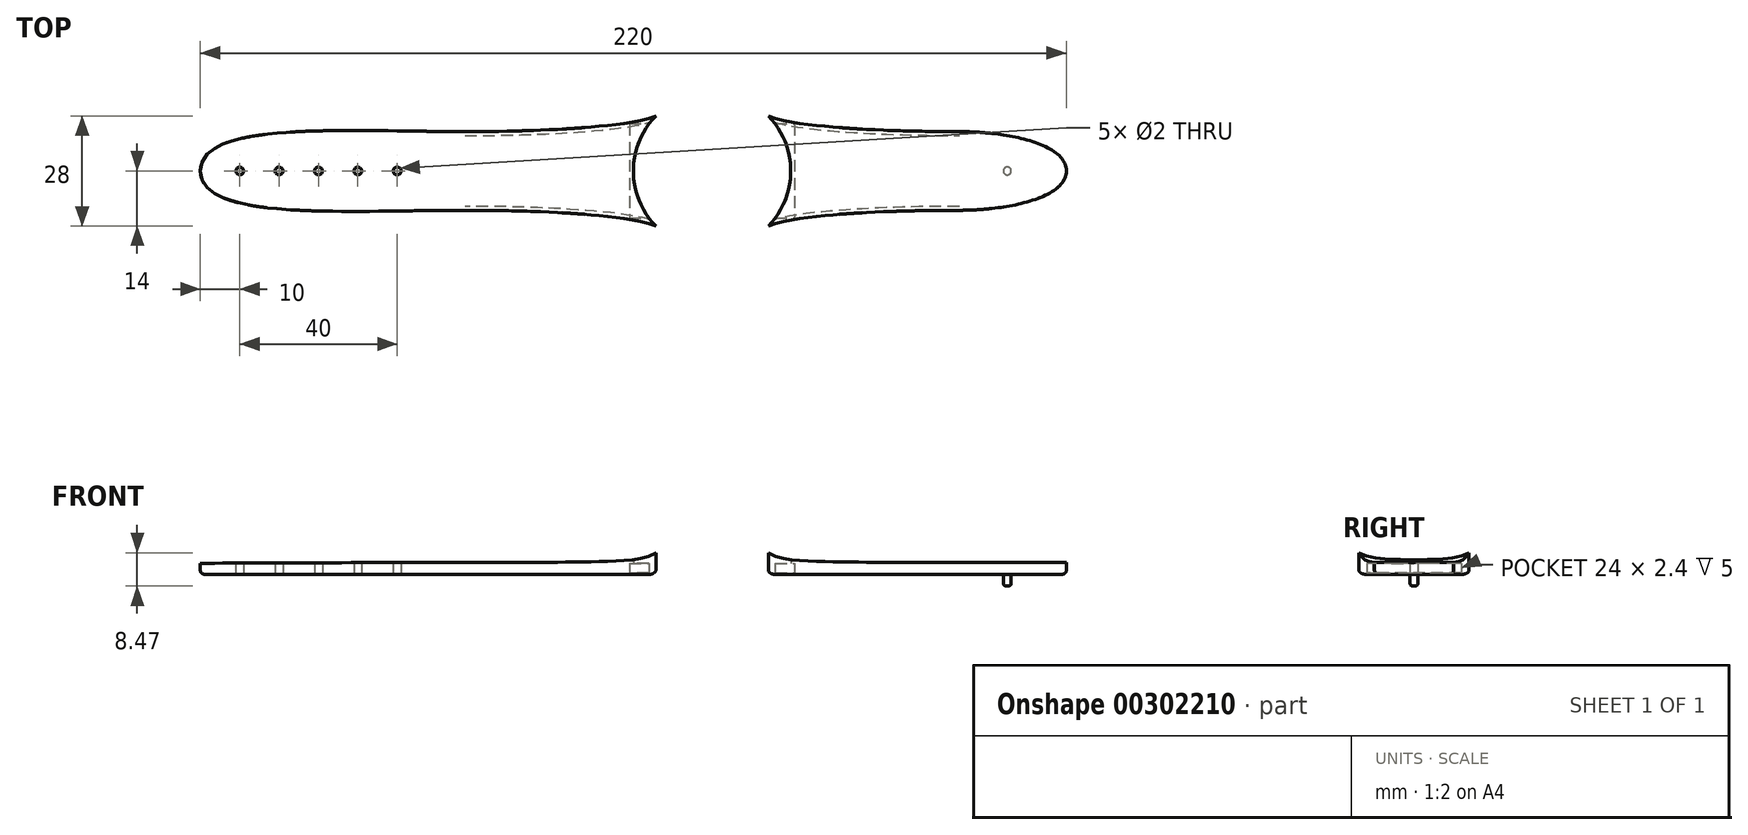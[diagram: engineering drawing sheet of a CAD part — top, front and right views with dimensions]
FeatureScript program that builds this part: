
annotation { "Feature Type Name" : "Feature", "Feature Type Description" : "" }
export const myFeature = defineFeature(function(context is Context, id is Id, definition is map)
    precondition{}
    {
        {
            var Q0;
            Q0=qCreatedBy(makeId("Top.planeOp"),FACE);
            var sketch = newSketch(context, id + "F0", { "sketchPlane" : qUnion([Q0])});
            skArc(sketch, "E0", {"start": v(-14.28, 14) * mm, "mid": v(-20, 0) * mm, "end": v(-14.28, -14) * mm});
            skFitSpline(sketch, "E1", {"points": [v(-14.28, 14) * mm, v(-62.8, 10) * mm], "startDerivative": vector(-9.22, -5.33) * mm, "endDerivative": vector(-87.74, 0) * mm});
            skLineSegment(sketch, "E2", {"start": v(-62.8, 10) * mm, "end": v(-62.8, 10) * mm});
            skFitSpline(sketch, "E3", {"points": [v(-62.8, 10) * mm, v(-130, 0) * mm], "startDerivative": vector(-91.88, 0) * mm, "endDerivative": vector(0, -38.55) * mm});
            skFitSpline(sketch, "E4.MirrorCS", {"points": [v(-14.28, -14) * mm, v(-62.8, -10) * mm], "startDerivative": vector(-9.22, 5.33) * mm, "endDerivative": vector(-87.74, 0) * mm});
            skLineSegment(sketch, "E5.MirrorCS", {"start": v(-62.8, -10) * mm, "end": v(-62.8, -10) * mm});
            skFitSpline(sketch, "E6.MirrorCS", {"points": [v(-62.8, -10) * mm, v(-130, 0) * mm], "startDerivative": vector(-91.88, 0) * mm, "endDerivative": vector(0, 38.55) * mm});
            skArc(sketch, "E7.MirrorCS", {"start": v(14.28, 14) * mm, "mid": v(20, 0) * mm, "end": v(14.28, -14) * mm});
            skFitSpline(sketch, "E8.MirrorCS", {"points": [v(14.28, 14) * mm, v(62.8, 10) * mm], "startDerivative": vector(9.22, -5.33) * mm, "endDerivative": vector(87.74, 0) * mm});
            skFitSpline(sketch, "E9.MirrorCS", {"points": [v(14.28, -14) * mm, v(62.8, -10) * mm], "startDerivative": vector(9.22, 5.33) * mm, "endDerivative": vector(87.74, 0) * mm});
            skLineSegment(sketch, "E10", {"start": v(62.8, 10) * mm, "end": v(62.8, 10) * mm});
            skLineSegment(sketch, "E11.MirrorCS", {"start": v(62.8, -10) * mm, "end": v(62.8, -10) * mm});
            skFitSpline(sketch, "E12.MirrorCS", {"points": [v(62.8, -10) * mm, v(90, 0) * mm], "startDerivative": vector(33.22, 0) * mm, "endDerivative": vector(0, 21.8) * mm});
            skFitSpline(sketch, "E13.MirrorCS", {"points": [v(62.8, 10) * mm, v(90, 0) * mm], "startDerivative": vector(33.22, 0) * mm, "endDerivative": vector(0, -21.8) * mm});
            skSolve(sketch);
        }
        {
            var Q0;
            Q0 = qSketchRegion(id + "F0", true);
            extrude(context, id + "F1", {"entities" : qUnion([Q0]), "depth" : (5.5) * mm});
        }
        {
            var Q0;
            Q0=qCreatedBy(makeId("Front.planeOp"),FACE);
            var sketch = newSketch(context, id + "F2", { "sketchPlane" : qUnion([Q0])});
            skLineSegment(sketch, "E14", {"start": v(-133.54, 2.78) * mm, "end": v(-133.54, 10.44) * mm});
            skLineSegment(sketch, "E15", {"start": v(-14.23, 5.5) * mm, "end": v(-25.17, 14.96) * mm});
            skLineSegment(sketch, "E16", {"start": v(-25.17, 14.96) * mm, "end": v(-133.54, 10.44) * mm});
            skLineSegment(sketch, "E17", {"start": v(14.23, 5.5) * mm, "end": v(22.62, 12.49) * mm});
            skLineSegment(sketch, "E18", {"start": v(22.62, 12.49) * mm, "end": v(93.9, 5.99) * mm});
            skPoint(sketch, "E19", {"position": v(-133.54, 2.78) * mm});
            skFitSpline(sketch, "E20.MirrorCS", {"points": [v(14.23, 5.5) * mm, v(80, 3) * mm], "startDerivative": vector(15.03, -7.53) * mm, "endDerivative": vector(188.68, 0) * mm});
            skFitSpline(sketch, "E21.MirrorCS", {"points": [v(-14.23, 5.5) * mm, v(-80, 3) * mm], "startDerivative": vector(-15.03, -7.53) * mm, "endDerivative": vector(-188.68, 0) * mm});
            skLineSegment(sketch, "E22.MirrorCS", {"start": v(-80, 3) * mm, "end": v(-133.54, 2.78) * mm});
            skLineSegment(sketch, "E23", {"start": v(80, 3) * mm, "end": v(80, 3) * mm});
            skLineSegment(sketch, "E24", {"start": v(80, 3) * mm, "end": v(92.32, 3) * mm});
            skLineSegment(sketch, "E25", {"start": v(92.32, 3) * mm, "end": v(93.9, 5.99) * mm});
            skSolve(sketch);
        }
        {
            var Q0;
            Q0 = qSketchRegion(id + "F2", true);
            extrude(context, id + "F3", {"entities" : qUnion([Q0]), "operationType" : NewBodyOperationType.REMOVE, "endBound" : BoundingType.SYMMETRIC, "oppositeDirection" : true, "depth" : 40 * mm});
        }
        {
            var Q0;
            Q0=makeQuery(id+"F3.boolean.opBoolean","INTERSECT",EDGE,{"derivedFrom":[makeQuery(id+"F1.opExtrude","SWEPT_FACE",FACE,{"disambiguationData":[OSD([sQuery(id+"F0.wireOp",EDGE,"E1")])]}),makeQuery(id+"F3.opExtrude","SWEPT_FACE",FACE,{"disambiguationData":[OSD([sQuery(id+"F2.wireOp",EDGE,"ddad4ba2-1875-45fb-a996-aad7ab552623")])]})]});
            var Q1;
            Q1=makeQuery(id+"F3.boolean.opBoolean","INTERSECT",EDGE,{"derivedFrom":[makeQuery(id+"F1.opExtrude","SWEPT_FACE",FACE,{"disambiguationData":[OSD([sQuery(id+"F0.wireOp",EDGE,"E3")])]}),makeQuery(id+"F3.opExtrude","SWEPT_FACE",FACE,{"disambiguationData":[OSD([sQuery(id+"F2.wireOp",EDGE,"ddad4ba2-1875-45fb-a996-aad7ab552623")])]})]});
            var Q2;
            Q2=makeQuery(id+"F1.opExtrude","CAP_EDGE",EDGE,{"disambiguationData":[OSD([sQuery(id+"F0.wireOp",EDGE,"E1")])],"isStart":true});
            var Q3;
            Q3=makeQuery(id+"F1.opExtrude","CAP_EDGE",EDGE,{"disambiguationData":[OSD([sQuery(id+"F0.wireOp",EDGE,"E8.MirrorCS")])],"isStart":true});
            var Q4;
            Q4=makeQuery(id+"F1.opExtrude","CAP_EDGE",EDGE,{"disambiguationData":[OSD([sQuery(id+"F0.wireOp",EDGE,"E9.MirrorCS")])],"isStart":true});
            var Q5;
            Q5=makeQuery(id+"F3.boolean.opBoolean","INTERSECT",EDGE,{"derivedFrom":[makeQuery(id+"F1.opExtrude","SWEPT_FACE",FACE,{"disambiguationData":[OSD([sQuery(id+"F0.wireOp",EDGE,"E8.MirrorCS")])]}),makeQuery(id+"F3.opExtrude","SWEPT_FACE",FACE,{"disambiguationData":[OSD([sQuery(id+"F2.wireOp",EDGE,"e5625134-0e9f-45f6-a949-9df659dbd201.MirrorCS")])]})]});
            fillet(context, id + "F4", {"entities" : qUnion([Q0, Q1, Q2, Q3, Q4, Q5]), "radius" : 1 * mm, "tangentPropagation" : true, "allowEdgeOverflow" : false});
        }
        {
            var Q0;
            Q0=qCreatedBy(makeId("Right.planeOp"),FACE);
            var sketch = newSketch(context, id + "F5", { "sketchPlane" : qUnion([Q0])});
            skLineSegment(sketch, "E26.bottom", {"start": v(12, 2.8) * mm, "end": v(-12, 2.8) * mm});
            skLineSegment(sketch, "E26.top", {"start": v(12, 0.4) * mm, "end": v(-12, 0.4) * mm});
            skLineSegment(sketch, "E26.left", {"start": v(12, 2.8) * mm, "end": v(12, 0.4) * mm});
            skLineSegment(sketch, "E26.right", {"start": v(-12, 2.8) * mm, "end": v(-12, 0.4) * mm});
            skSolve(sketch);
        }
        {
            var Q0;
            Q0 = qSketchRegion(id + "F5", true);
            extrude(context, id + "F6", {"entities" : qUnion([Q0]), "operationType" : NewBodyOperationType.REMOVE, "endBound" : BoundingType.SYMMETRIC, "oppositeDirection" : true, "depth" : 42 * mm});
        }
        {
            var Q0;
            Q0=makeQuery(id+"F1.opExtrude","CAP_FACE",FACE,{"disambiguationData":[OSD([sQuery(id+"F0.wireOp",EDGE,"E7.MirrorCS"),sQuery(id+"F0.wireOp",EDGE,"E8.MirrorCS"),sQuery(id+"F0.wireOp",EDGE,"E9.MirrorCS"),sQuery(id+"F0.wireOp",EDGE,"E12.MirrorCS"),sQuery(id+"F0.wireOp",EDGE,"E13.MirrorCS")])],"isStart":true});
            var sketch = newSketch(context, id + "F7", { "sketchPlane" : qUnion([Q0])});
            skCircle(sketch, "E27", {"center": v(75, 0) * mm, "radius": 1 * mm});
            skSolve(sketch);
        }
        {
            var Q0;
            Q0=makeQuery(id+"F7.imprint","IMPRINT",FACE,{"disambiguationData":[TD([[makeQuery(id+"F7.imprint","IMPRINT",EDGE,{"derivedFrom":sQuery(id+"F7.wireOp",EDGE,"E27")}),1.0]])]});
            extrude(context, id + "F8", {"entities" : qUnion([Q0]), "operationType" : NewBodyOperationType.ADD, "depth" : 3 * mm});
        }
        {
            var Q0;
            Q0=makeQuery(id+"F8.opExtrude","CAP_FACE",FACE,{"disambiguationData":[OSD([sQuery(id+"F7.wireOp",EDGE,"E27")])],"isStart":false});
            fillet(context, id + "F9", {"entities" : qUnion([Q0]), "radius" : 0.7 * mm, "tangentPropagation" : true, "allowEdgeOverflow" : false});
        }
        {
            var Q0;
            Q0=makeQuery(id+"F1.opExtrude","CAP_FACE",FACE,{"disambiguationData":[OSD([sQuery(id+"F0.wireOp",EDGE,"E0"),sQuery(id+"F0.wireOp",EDGE,"E1"),sQuery(id+"F0.wireOp",EDGE,"E3"),sQuery(id+"F0.wireOp",EDGE,"E4.MirrorCS"),sQuery(id+"F0.wireOp",EDGE,"E6.MirrorCS")])],"isStart":true});
            var sketch = newSketch(context, id + "F10", { "sketchPlane" : qUnion([Q0])});
            skPoint(sketch, "E28", {"position": v(-80, 0) * mm});
            skPoint(sketch, "E29", {"position": v(-90, 0) * mm});
            skPoint(sketch, "E30", {"position": v(-100, 0) * mm});
            skPoint(sketch, "E31", {"position": v(-110, 0) * mm});
            skPoint(sketch, "E32", {"position": v(-120, 0) * mm});
            skSolve(sketch);
        }
        {
            var Q0;
            Q0=sQuery(id+"F10.wireOp",VERTEX,"E32");
            var Q1;
            Q1=sQuery(id+"F10.wireOp",VERTEX,"E31");
            var Q2;
            Q2=sQuery(id+"F10.wireOp",VERTEX,"E30");
            var Q3;
            Q3=sQuery(id+"F10.wireOp",VERTEX,"E29");
            var Q4;
            Q4=sQuery(id+"F10.wireOp",VERTEX,"E28");
            var Q5;
            Q5=makeQuery(id+"F1.opExtrude","SWEPT_BODY",BODY,{"disambiguationData":[OSD([sQuery(id+"F0.wireOp",EDGE,"E0"),sQuery(id+"F0.wireOp",EDGE,"E1"),sQuery(id+"F0.wireOp",EDGE,"E3"),sQuery(id+"F0.wireOp",EDGE,"E4.MirrorCS"),sQuery(id+"F0.wireOp",EDGE,"E6.MirrorCS")])]});
            hole(context, id + "F11", {"style" : HoleStyle.SIMPLE, "endStyle" : HoleEndStyle.THROUGH, "holeDiameter" : 2 * mm, "isTappedThrough" : true, "tappedDepth" : 12 * mm, "tapClearance" : 3, "locations" : qUnion([Q0, Q1, Q2, Q3, Q4]), "scope" : qUnion([Q5])});
        }
    });
